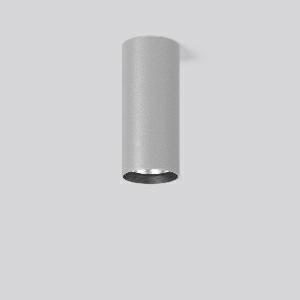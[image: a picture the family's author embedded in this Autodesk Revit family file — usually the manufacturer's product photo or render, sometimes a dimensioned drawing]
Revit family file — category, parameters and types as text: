
# Revit family: heledon_mini_a_931200_004_3_e82d
name_source: partatom
category: Lighting Fixtures
units: mm (PartAtom-declared; Revit-internal decimal feet)

## family parameters
Cut with Voids When Loaded = No
Host = Face
Light Source = No
Part Type = Normal
Room Calculation Point = No
Round Connector Dimension = Use Diameter
Shared = No

## types (1)
- HELEDON mini A (1 x LED Modul 935, 2600 lm, 3500)
    Apparent Load = 20 VA
    Approval mark = CE
    CIE Flux Codes = 100 100 100 100 100
    Color Rendering = 92
    Color Temperature = 3500
    Default Elevation = 1800 mm
    Description = Series: HELEDON mini
Cylindrical surface-mounted downlight. Housing: die-cast aluminium, powder-coated. Internal ceiling frame polycarbonate with bayonet mounting. Black plastic ring and recessed LED to prevent glare from the side. Optical assembly with reflector made of MIRO-Silver with 98% total light reflection for outstanding efficiency - can be changed without tools. Best colour rendering index Ra>90. Suitable for Ceiling mounting. Easy installation with a separate ceiling frame with bayonet mounting and plug connection. Driver integrated. Connected via plug-in connector. High quality converter without flickering and stroboscopic effect. The following accessories can be mounted without use of tools: interchangeable lenses, decorative glasses, honeycomb louvre, clear and frosted diffusers, white interchangeable plastic ring. 
Colour: silver
Diameter: 87 mm
Height: 197 mm
Lamp: LED
Socket: without socket
Colour temperature: 3500K
Colour rendering index (CRI): 92
System power: 20 W
Rated luminous flux: 2600 lm
Luminous efficiency: 130 lm/W
Control gear: Regulated power supply
Protection class: I
Type of protection: IP 20
    Height = 197 mm
    Lamp = 1 x LED Modul 935
    Lamp Light Flux = 2600 lm
    Lamp count = 1
    Length = 87 mm
    Lifetime = 50000 h
    Luminous efficacy = 130 lm/W
    Manufacturer = RZB
    ModVariant = No
    Model = 931200.004.3
    Mounting Place = Ceiling
    Mounting Type = Surface mounted
    Number of Poles = 1
    OnlyDefault = Yes
    Power Factor = 1
    Product Name = HELEDON mini A
    Product group = Surface mounted downlights
    ProductGroupID = 302
    Protection Class = Protection class I
    Protection Degree = IP 20
    RLX_Detail_Level = 1
    RLX_Emergency_Light_Flux = 0 lm
    RLX_Emergency_Type = 0
    RLX_Emergency_Type_DB = No
    RlxData = <blob elided: 109485 chars, md5=dabe98a8>
    Socket = socket
    Standby Power = 0 W
    System Light Flux = 2600 lm
    System Power = 20 W
    Type Comments = Product without accessories
    Type Image = 931188.004.jpg
    URL = http://relux.com
    VarID = ---
    Voltage = 230 V
    Voltage Range = 220-240 V
    Weight = 0.00 kg
    Width = 0 mm  [stored 0 ft]

note: [stored X ft] marks values corroborated as IEEE doubles in the binary element streams (Revit-internal decimal feet)

## geometry (parser evidence)
native form markers: Blend x4, Sweep x8
no freeform markers — native parametric forms only
